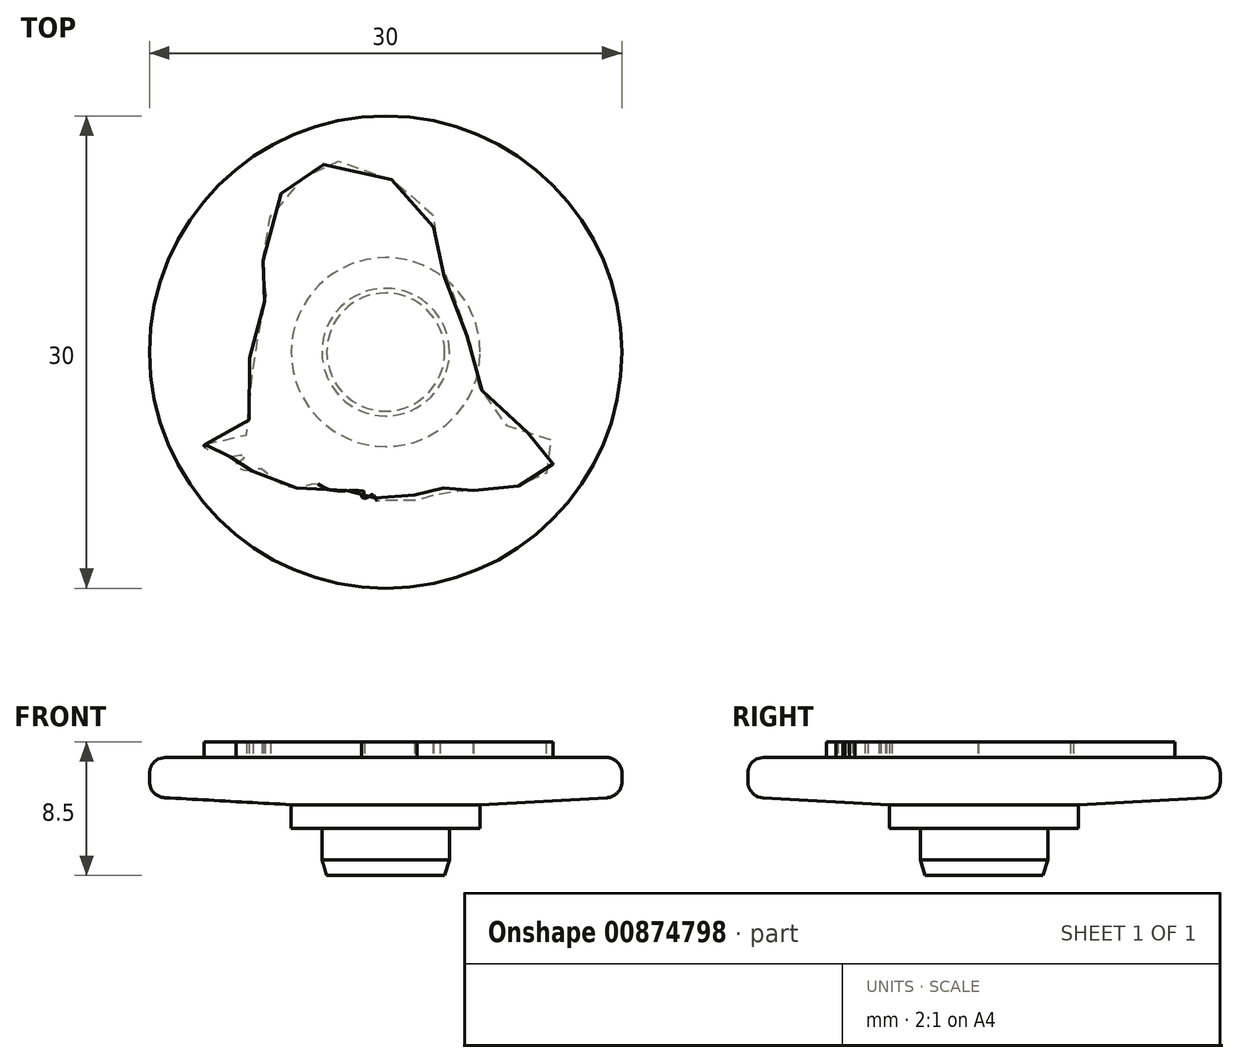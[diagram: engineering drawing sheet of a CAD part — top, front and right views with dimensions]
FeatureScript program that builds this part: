
annotation { "Feature Type Name" : "Feature", "Feature Type Description" : "" }
export const myFeature = defineFeature(function(context is Context, id is Id, definition is map)
    precondition{}
    {
        {
            var Q0;
            Q0=qCreatedBy(makeId("Front.planeOp"),FACE);
            var sketch = newSketch(context, id + "F0", { "sketchPlane" : qUnion([Q0])});
            skLineSegment(sketch, "E0", {"start": v(0, -3.57) * mm, "end": v(0, 7.5) * mm, "construction": true});
            skLineSegment(sketch, "E1", {"start": v(0, 0) * mm, "end": v(4.05, 0) * mm});
            skLineSegment(sketch, "E2", {"start": v(4.05, 0) * mm, "end": v(4.05, 3) * mm});
            skLineSegment(sketch, "E3", {"start": v(4.05, 3) * mm, "end": v(6, 3) * mm});
            skLineSegment(sketch, "E4", {"start": v(15, 5) * mm, "end": v(15, 7.5) * mm});
            skLineSegment(sketch, "E5.trimOffspring", {"start": v(0, 7.5) * mm, "end": v(0, 0) * mm});
            skPoint(sketch, "E6.start.orphan", {"position": v(0, 7.5) * mm});
            skLineSegment(sketch, "E7", {"start": v(15, 7.5) * mm, "end": v(0, 7.5) * mm});
            skLineSegment(sketch, "E8", {"start": v(6, 3) * mm, "end": v(6, 4.5) * mm});
            skLineSegment(sketch, "E9", {"start": v(6, 4.5) * mm, "end": v(15, 5) * mm});
            skSolve(sketch);
        }
        {
            var Q0;
            Q0=qSketchRegion(id+"F0",true);
            var Q1;
            Q1=sQuery(id+"F0.wireOp",EDGE,"E0");
            revolve(context, id + "F1", {"surfaceOperationType" : NewSurfaceOperationType.NEW, "entities" : qUnion([Q0]), "axis" : qUnion([Q1]), "revolveType" : RevolveType.FULL});
        }
        {
            var Q0;
            Q0=makeQuery(id+"F1.opRevolve","SWEPT_EDGE",EDGE,{"disambiguationData":[OSD([sQuery(id+"F0.wireOp",EDGE,"E4"),sQuery(id+"F0.wireOp",EDGE,"33tfvtyz-JtyN-Mw5L-3XGJ-TJyQ87O0g8P3")])]});
            var Q1;
            Q1=makeQuery(id+"F1.opRevolve","SWEPT_EDGE",EDGE,{"disambiguationData":[OSD([sQuery(id+"F0.wireOp",EDGE,"Du0anDyR-X8kC-RIz2-9by8-a22dYFmIHx84"),sQuery(id+"F0.wireOp",EDGE,"E4")])]});
            fillet(context, id + "F2", {"entities" : qUnion([Q0, Q1]), "radius" : 1 * mm, "tangentPropagation" : true, "allowEdgeOverflow" : false});
        }
        {
            var Q0;
            Q0=makeQuery(id+"F1.opRevolve","SWEPT_EDGE",EDGE,{"disambiguationData":[OSD([sQuery(id+"F0.wireOp",EDGE,"E1"),sQuery(id+"F0.wireOp",EDGE,"E2")])]});
            chamfer(context, id + "F3", {"entities" : qUnion([Q0]), "chamferType" : ChamferType.TWO_OFFSETS, "width1" : .3 * mm, "oppositeDirection" : false, "width2" : 1 * mm, "tangentPropagation" : true});
        }
        {
            var Q0;
            Q0=makeQuery(id+"F1.opRevolve","SWEPT_FACE",FACE,{"disambiguationData":[OSD([sQuery(id+"F0.wireOp",EDGE,"E7")])]});
            var sketch = newSketch(context, id + "F4", { "sketchPlane" : qUnion([Q0])});
            skFitSpline(sketch, "E10", {"points": [v(-11.46, -5.86) * mm, v(-9.63, -5.99) * mm, v(-9.06, -5.82) * mm, v(-8.74, -4.76) * mm, v(-8.6, -3.08) * mm, v(-8.45, -1.1) * mm, v(-8.48, -0.38) * mm, v(-8.67, -0.36) * mm, v(-8.07, 0.94) * mm, v(-7.66, 2.1) * mm, v(-7.7, 3.06) * mm, v(-7.4, 4.24) * mm, v(-7.4, 5.67) * mm, v(-7.67, 5.5) * mm, v(-7.85, 5.56) * mm, v(-7.68, 6.1) * mm, v(-7.52, 7.13) * mm, v(-7.21, 9.04) * mm, v(-6.14, 10.57) * mm, v(-5.29, 11.04) * mm, v(-4.61, 11.52) * mm, v(-4.48, 11.6) * mm, v(-3.7, 12.03) * mm, v(-2.21, 12.03) * mm, v(-0.57, 11.5) * mm, v(1.17, 10.45) * mm, v(2.54, 9.47) * mm, v(3.01, 8.58) * mm, v(3.06, 7.29) * mm, v(3.45, 6.2) * mm, v(3.45, 5.5) * mm, v(3.64, 5.18) * mm, v(3.76, 4.5) * mm, v(4.5, 3.22) * mm, v(4.88, 1.91) * mm, v(5.32, 0.68) * mm, v(5.57, 0) * mm, v(5.57, -1.13) * mm, v(6.02, -2.36) * mm, v(6.63, -2.95) * mm, v(7.34, -4.34) * mm, v(8.51, -5) * mm, v(10.38, -5.35) * mm, v(10.55, -5.44) * mm, v(10.17, -6.17) * mm, v(10.55, -6.8) * mm, v(10.45, -7.61) * mm, v(9.8, -7.76) * mm, v(9.73, -8.14) * mm, v(9.2, -8.18) * mm, v(8.23, -8.54) * mm, v(7.68, -8.31) * mm, v(6.6, -8.3) * mm, v(5.9, -8.79) * mm, v(5.59, -8.79) * mm, v(5.44, -8.4) * mm, v(4.83, -8.4) * mm, v(4.58, -8.87) * mm, v(4, -8.9) * mm, v(3.67, -8.62) * mm, v(3.21, -8.75) * mm, v(2.98, -9.15) * mm, v(2.56, -9.38) * mm, v(2.32, -8.98) * mm, v(1.84, -9.04) * mm, v(1.98, -9.45) * mm, v(1.42, -9.87) * mm, v(0, -9.9) * mm, v(-0.69, -9.25) * mm, v(-0.91, -9.04) * mm, v(-1.27, -9.28) * mm, v(-1.54, -9.11) * mm, v(-1.35, -8.9) * mm, v(-2.17, -8.79) * mm, v(-3.04, -8.83) * mm, v(-3.9, -8.62) * mm, v(-4.41, -8.37) * mm, v(-5.53, -8.62) * mm, v(-6.27, -8.52) * mm, v(-7.28, -7.93) * mm, v(-7.97, -7.38) * mm, v(-8.33, -7.53) * mm, v(-9.26, -7.42) * mm, v(-9.5, -7.1) * mm, v(-8.84, -6.6) * mm, v(-9.47, -6.6) * mm, v(-10.1, -6.66) * mm, v(-10.4, -6.4) * mm, v(-10.7, -6.21) * mm, v(-11.25, -6.23) * mm, v(-11.49, -6.02) * mm, v(-11.54, -5.95) * mm, v(-11.46, -5.86) * mm]});
            skSolve(sketch);
        }
        {
            var Q0;
            Q0=makeQuery(id+"F4.imprint","IMPRINT",FACE,{"disambiguationData":[TD([[makeQuery(id+"F4.imprint","IMPRINT",EDGE,{"derivedFrom":sQuery(id+"F4.wireOp",EDGE,"E10")}),-1.0]])]});
            extrude(context, id + "F5", {"entities" : qUnion([Q0]), "operationType" : NewBodyOperationType.ADD, "depth" : 1 * mm, "offsetDistance" : 25 * mm});
        }
    });
